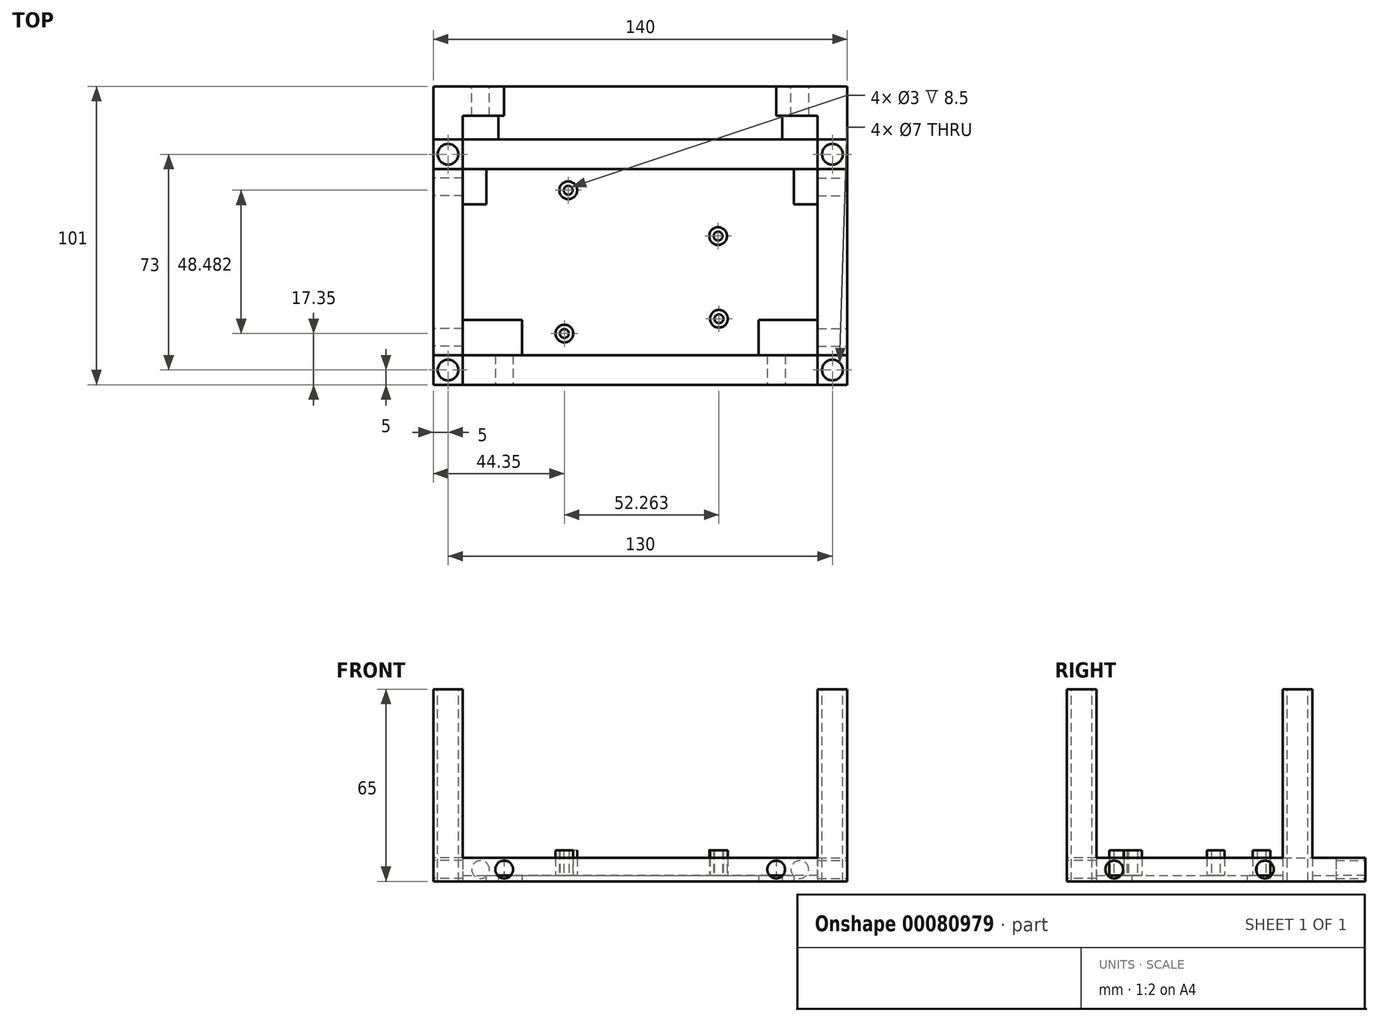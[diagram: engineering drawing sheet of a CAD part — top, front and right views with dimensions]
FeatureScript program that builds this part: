
annotation { "Feature Type Name" : "Feature", "Feature Type Description" : "" }
export const myFeature = defineFeature(function(context is Context, id is Id, definition is map)
    precondition{}
    {
        {
            var Q0;
            Q0=qCreatedBy(makeId("Top.planeOp"),FACE);
            var sketch = newSketch(context, id + "F0", { "sketchPlane" : qUnion([Q0])});
            skLineSegment(sketch, "E0.bottom", {"start": v(-70, 50) * mm, "end": v(70, 50) * mm, "construction": true});
            skLineSegment(sketch, "E0.top", {"start": v(-70, -50) * mm, "end": v(70, -50) * mm, "construction": true});
            skLineSegment(sketch, "E0.left", {"start": v(-70, 50) * mm, "end": v(-70, -50) * mm, "construction": true});
            skLineSegment(sketch, "E0.right", {"start": v(70, 50) * mm, "end": v(70, -50) * mm, "construction": true});
            skPoint(sketch, "E0.middle", {"position": v(0, 0) * mm});
            skLineSegment(sketch, "E1", {"start": v(-70, 50) * mm, "end": v(-70, 33) * mm});
            skLineSegment(sketch, "E2.bottom", {"start": v(-70, 33) * mm, "end": v(-60, 33) * mm});
            skLineSegment(sketch, "E2.top", {"start": v(-70, 23) * mm, "end": v(-60, 23) * mm});
            skLineSegment(sketch, "E2.left", {"start": v(-70, 33) * mm, "end": v(-70, 23) * mm});
            skLineSegment(sketch, "E2.right", {"start": v(-60, 33) * mm, "end": v(-60, 23) * mm});
            skLineSegment(sketch, "E3", {"start": v(70, 50) * mm, "end": v(70, 33) * mm});
            skLineSegment(sketch, "E4.bottom", {"start": v(70, 33) * mm, "end": v(60, 33) * mm});
            skLineSegment(sketch, "E4.top", {"start": v(70, 23) * mm, "end": v(60, 23) * mm});
            skLineSegment(sketch, "E4.left", {"start": v(70, 33) * mm, "end": v(70, 23) * mm});
            skLineSegment(sketch, "E4.right", {"start": v(60, 33) * mm, "end": v(60, 23) * mm});
            skLineSegment(sketch, "E5.bottom", {"start": v(-70, -50) * mm, "end": v(-60, -50) * mm});
            skLineSegment(sketch, "E5.top", {"start": v(-70, -40) * mm, "end": v(-60, -40) * mm});
            skLineSegment(sketch, "E5.left", {"start": v(-70, -50) * mm, "end": v(-70, -40) * mm});
            skLineSegment(sketch, "E5.right", {"start": v(-60, -50) * mm, "end": v(-60, -40) * mm});
            skLineSegment(sketch, "E6.bottom", {"start": v(70, -50) * mm, "end": v(60, -50) * mm});
            skLineSegment(sketch, "E6.top", {"start": v(70, -40) * mm, "end": v(60, -40) * mm});
            skLineSegment(sketch, "E6.left", {"start": v(70, -50) * mm, "end": v(70, -40) * mm});
            skLineSegment(sketch, "E6.right", {"start": v(60, -50) * mm, "end": v(60, -40) * mm});
            skSolve(sketch);
        }
        {
            var Q0;
            Q0=qSketchRegion(id+"F0",true);
            extrude(context, id + "F1", {"entities" : qUnion([Q0]), "oppositeDirection" : true, "depth" : 60 * mm});
        }
        {
            var Q0;
            Q0=qCreatedBy(makeId("Top.planeOp"),FACE);
            cPlane(context, id + "F2", {"entities" : qUnion([Q0]), "cplaneType" : CPlaneType.OFFSET, "offset" : 65 * mm, "oppositeDirection" : true, "width" : 150 * mm, "height" : 150 * mm});
        }
        {
            var Q0;
            Q0=qCreatedBy(id+"F2.planeOp",FACE);
            var sketch = newSketch(context, id + "F3", { "sketchPlane" : qUnion([Q0])});
            skLineSegment(sketch, "E7.0", {"start": v(-70, 33) * mm, "end": v(-60, 33) * mm});
            skLineSegment(sketch, "E8.0", {"start": v(-70, 33) * mm, "end": v(-70, 23) * mm});
            skLineSegment(sketch, "E9.0", {"start": v(-70, -50) * mm, "end": v(-70, -40) * mm});
            skLineSegment(sketch, "E10.0", {"start": v(-70, -50) * mm, "end": v(-60, -50) * mm});
            skLineSegment(sketch, "E11.0", {"start": v(70, -50) * mm, "end": v(60, -50) * mm});
            skLineSegment(sketch, "E12.0", {"start": v(70, -50) * mm, "end": v(70, -40) * mm});
            skLineSegment(sketch, "E13.0", {"start": v(70, 33) * mm, "end": v(70, 23) * mm});
            skLineSegment(sketch, "E14.0.0", {"start": v(70, 23) * mm, "end": v(70, 33) * mm});
            skLineSegment(sketch, "E14.0.1", {"start": v(70, 33) * mm, "end": v(60, 33) * mm});
            skLineSegment(sketch, "E15.0.0", {"start": v(-60, 33) * mm, "end": v(-70, 33) * mm});
            skLineSegment(sketch, "E16.0.0", {"start": v(-70, -40) * mm, "end": v(-70, -50) * mm});
            skLineSegment(sketch, "E17.0.0", {"start": v(60, -50) * mm, "end": v(70, -50) * mm});
            skLineSegment(sketch, "E18", {"start": v(-60, -50) * mm, "end": v(60, -50) * mm});
            skLineSegment(sketch, "E19", {"start": v(70, -40) * mm, "end": v(70, 23) * mm});
            skLineSegment(sketch, "E20", {"start": v(60, 33) * mm, "end": v(-60, 33) * mm});
            skLineSegment(sketch, "E21", {"start": v(-60, 23) * mm, "end": v(60, 23) * mm});
            skLineSegment(sketch, "E22", {"start": v(60, -40) * mm, "end": v(60, 23) * mm});
            skLineSegment(sketch, "E23", {"start": v(60, -40) * mm, "end": v(-60, -40) * mm});
            skLineSegment(sketch, "E24", {"start": v(-60, -40) * mm, "end": v(-60, 23) * mm});
            skLineSegment(sketch, "E25", {"start": v(-70, 23) * mm, "end": v(-70, -40) * mm});
            skPoint(sketch, "E14.0.2.end.orphan", {"position": v(60, 23) * mm});
            skLineSegment(sketch, "E26.top", {"start": v(-70, 51) * mm, "end": v(-60, 51) * mm});
            skLineSegment(sketch, "E26.left", {"start": v(-70, 33) * mm, "end": v(-70, 51) * mm});
            skLineSegment(sketch, "E26.right", {"start": v(-60, 33) * mm, "end": v(-60, 51) * mm});
            skLineSegment(sketch, "E27.top", {"start": v(70, 51) * mm, "end": v(60, 51) * mm});
            skLineSegment(sketch, "E27.left", {"start": v(70, 33) * mm, "end": v(70, 51) * mm});
            skLineSegment(sketch, "E27.right", {"start": v(60, 33) * mm, "end": v(60, 51) * mm});
            skLineSegment(sketch, "E28.bottom", {"start": v(-70, 51) * mm, "end": v(-46, 51) * mm});
            skLineSegment(sketch, "E28.top", {"start": v(-70, 41) * mm, "end": v(-46, 41) * mm});
            skLineSegment(sketch, "E28.left", {"start": v(-70, 51) * mm, "end": v(-70, 41) * mm});
            skLineSegment(sketch, "E28.right", {"start": v(-46, 51) * mm, "end": v(-46, 41) * mm});
            skLineSegment(sketch, "E29.bottom", {"start": v(70, 51) * mm, "end": v(46, 51) * mm});
            skLineSegment(sketch, "E29.top", {"start": v(70, 41) * mm, "end": v(46, 41) * mm});
            skLineSegment(sketch, "E29.left", {"start": v(70, 51) * mm, "end": v(70, 41) * mm});
            skLineSegment(sketch, "E29.right", {"start": v(46, 51) * mm, "end": v(46, 41) * mm});
            skSolve(sketch);
        }
        {
            var Q0;
            Q0=qSketchRegion(id+"F3",true);
            extrude(context, id + "F4", {"entities" : qUnion([Q0]), "operationType" : NewBodyOperationType.ADD, "depth" : 8 * mm});
        }
        {
            var Q0;
            Q0=qCreatedBy(id+"F2.planeOp",FACE);
            var sketch = newSketch(context, id + "F5", { "sketchPlane" : qUnion([Q0])});
            skPoint(sketch, "E30.0", {"position": v(-70, 33) * mm});
            skPoint(sketch, "E31.0", {"position": v(70, 33) * mm});
            skPoint(sketch, "E32.0", {"position": v(70, -50) * mm});
            skPoint(sketch, "E33.0", {"position": v(-70, -50) * mm});
            skPoint(sketch, "E34.0", {"position": v(-60, -40) * mm});
            skPoint(sketch, "E35.0", {"position": v(-60, 23) * mm});
            skPoint(sketch, "E36.0", {"position": v(60, 23) * mm});
            skPoint(sketch, "E37.0", {"position": v(60, -40) * mm});
            skLineSegment(sketch, "E38.bottom", {"start": v(-52, 33) * mm, "end": v(-48, 33) * mm});
            skLineSegment(sketch, "E39.top", {"start": v(60, -28) * mm, "end": v(40, -28) * mm});
            skLineSegment(sketch, "E39.right", {"start": v(40, -40) * mm, "end": v(40, -28) * mm});
            skLineSegment(sketch, "E40.top", {"start": v(60, 11) * mm, "end": v(52, 11) * mm});
            skLineSegment(sketch, "E41.top", {"start": v(-60, 11) * mm, "end": v(-52, 11) * mm});
            skLineSegment(sketch, "E42.top", {"start": v(-60, -28) * mm, "end": v(-40, -28) * mm});
            skLineSegment(sketch, "E42.right", {"start": v(-40, -40) * mm, "end": v(-40, -28) * mm});
            skLineSegment(sketch, "E43.0", {"start": v(-60, 41) * mm, "end": v(-46, 41) * mm});
            skLineSegment(sketch, "E44.0", {"start": v(-46, 51) * mm, "end": v(-46, 41) * mm});
            skLineSegment(sketch, "E45.0", {"start": v(46, 51) * mm, "end": v(46, 41) * mm});
            skLineSegment(sketch, "E46", {"start": v(-48, 33) * mm, "end": v(-48, 41) * mm});
            skLineSegment(sketch, "E47", {"start": v(-46, 51) * mm, "end": v(46, 51) * mm});
            skLineSegment(sketch, "E48", {"start": v(48, 33) * mm, "end": v(48, 41) * mm});
            skLineSegment(sketch, "E49", {"start": v(48, 33) * mm, "end": v(52, 33) * mm});
            skPoint(sketch, "E50.end.orphan", {"position": v(60, 41) * mm});
            skLineSegment(sketch, "E51", {"start": v(-60, -28) * mm, "end": v(-60, 11) * mm});
            skLineSegment(sketch, "E52", {"start": v(60, -28) * mm, "end": v(60, 11) * mm});
            skLineSegment(sketch, "E53", {"start": v(52, 33) * mm, "end": v(52, 11) * mm});
            skLineSegment(sketch, "E54", {"start": v(-52, 11) * mm, "end": v(-52, 33) * mm});
            skLineSegment(sketch, "E55", {"start": v(-40, -40) * mm, "end": v(40, -40) * mm});
            skLineSegment(sketch, "E56", {"start": v(46, 41) * mm, "end": v(48, 41) * mm});
            skLineSegment(sketch, "E57", {"start": v(-48, 41) * mm, "end": v(-46, 41) * mm});
            skSolve(sketch);
        }
        {
            var Q0;
            Q0=qSketchRegion(id+"F5",true);
            extrude(context, id + "F6", {"entities" : qUnion([Q0]), "operationType" : NewBodyOperationType.ADD, "depth" : 2 * mm});
        }
        {
            var Q0;
            Q0=qCreatedBy(id+"F2.planeOp",FACE);
            var sketch = newSketch(context, id + "F7", { "sketchPlane" : qUnion([Q0])});
            skLineSegment(sketch, "E58", {"start": v(-24.36, -18.42) * mm, "end": v(-24.36, -17.12) * mm, "construction": true});
            skPoint(sketch, "E59.middle", {"position": v(0, -8.5) * mm});
            skCircle(sketch, "E60", {"center": v(-24.35, 15.83) * mm, "radius": 1.5 * mm});
            skCircle(sketch, "E61", {"center": v(-25.65, -32.65) * mm, "radius": 1.5 * mm});
            skCircle(sketch, "E62", {"center": v(26.34, 0.33) * mm, "radius": 1.5 * mm});
            skCircle(sketch, "E63", {"center": v(26.61, -27.67) * mm, "radius": 1.5 * mm});
            skCircle(sketch, "E64", {"center": v(-24.35, 15.83) * mm, "radius": 3 * mm});
            skCircle(sketch, "E65", {"center": v(26.34, 0.33) * mm, "radius": 3 * mm});
            skCircle(sketch, "E66", {"center": v(26.61, -27.67) * mm, "radius": 3 * mm});
            skCircle(sketch, "E67", {"center": v(-25.65, -32.65) * mm, "radius": 3 * mm});
            skLineSegment(sketch, "E68", {"start": v(-24.35, 15.83) * mm, "end": v(26.34, 0.33) * mm, "construction": true});
            skLineSegment(sketch, "E69", {"start": v(26.34, 0.33) * mm, "end": v(26.61, -27.67) * mm, "construction": true});
            skLineSegment(sketch, "E70", {"start": v(26.61, -27.67) * mm, "end": v(-25.65, -32.65) * mm, "construction": true});
            skLineSegment(sketch, "E71", {"start": v(-25.65, -32.65) * mm, "end": v(-24.35, 15.83) * mm, "construction": true});
            skLineSegment(sketch, "E72", {"start": v(-24.35, 15.83) * mm, "end": v(26.61, -27.67) * mm, "construction": true});
            skLineSegment(sketch, "E73", {"start": v(26.34, 0.33) * mm, "end": v(-25.65, -32.65) * mm, "construction": true});
            skSolve(sketch);
        }
        {
            var Q0;
            Q0 = qSketchRegion(id + "F7", true);
            extrude(context, id + "F8", {"entities" : qUnion([Q0]), "operationType" : NewBodyOperationType.ADD, "depth" : 10.5 * mm});
        }
        {
            var Q0;
            Q0=qCreatedBy(makeId("Top.planeOp"),FACE);
            var sketch = newSketch(context, id + "F9", { "sketchPlane" : qUnion([Q0])});
            skLineSegment(sketch, "E74.0", {"start": v(-60, 33) * mm, "end": v(-60, 23) * mm});
            skLineSegment(sketch, "E75.0", {"start": v(-70, 23) * mm, "end": v(-60, 23) * mm});
            skLineSegment(sketch, "E76.0", {"start": v(-70, -40) * mm, "end": v(-60, -40) * mm});
            skLineSegment(sketch, "E77.0", {"start": v(-60, -50) * mm, "end": v(-60, -40) * mm});
            skLineSegment(sketch, "E78.0", {"start": v(60, -50) * mm, "end": v(60, -40) * mm});
            skLineSegment(sketch, "E79.0", {"start": v(70, -40) * mm, "end": v(60, -40) * mm});
            skLineSegment(sketch, "E80.0", {"start": v(70, 23) * mm, "end": v(60, 23) * mm});
            skLineSegment(sketch, "E81.0", {"start": v(60, 33) * mm, "end": v(60, 23) * mm});
            skCircle(sketch, "E82", {"center": v(-65, 28) * mm, "radius": 3.5 * mm});
            skPoint(sketch, "E82.centerSnap0", {"position": v(-60, 28) * mm});
            skPoint(sketch, "E82.centerSnap1", {"position": v(-65, 23) * mm});
            skCircle(sketch, "E83", {"center": v(-65, -45) * mm, "radius": 3.5 * mm});
            skPoint(sketch, "E83.centerSnap0", {"position": v(-60, -45) * mm});
            skPoint(sketch, "E83.centerSnap1", {"position": v(-65, -40) * mm});
            skCircle(sketch, "E84", {"center": v(65, -45) * mm, "radius": 3.5 * mm});
            skPoint(sketch, "E84.centerSnap0", {"position": v(60, -45) * mm});
            skPoint(sketch, "E84.centerSnap1", {"position": v(65, -40) * mm});
            skCircle(sketch, "E85", {"center": v(65, 28) * mm, "radius": 3.5 * mm});
            skPoint(sketch, "E85.centerSnap0", {"position": v(65, 23) * mm});
            skPoint(sketch, "E85.centerSnap1", {"position": v(60, 28) * mm});
            skSolve(sketch);
        }
        {
            var Q0;
            Q0 = qSketchRegion(id + "F9", true);
            extrude(context, id + "F10", {"entities" : qUnion([Q0]), "operationType" : NewBodyOperationType.REMOVE, "oppositeDirection" : true, "depth" : 75 * mm});
        }
        {
            var Q0;
            Q0=makeQuery(id+"F4.boolean.opBoolean","MERGE",FACE,{"derivedFrom":[makeQuery(id+"F1.opExtrude","SWEPT_FACE",FACE,{"disambiguationData":[OSD([sQuery(id+"F0.wireOp",EDGE,"E4.left")])]}),makeQuery(id+"F1.opExtrude","SWEPT_FACE",FACE,{"disambiguationData":[OSD([sQuery(id+"F0.wireOp",EDGE,"E6.left")])]}),makeQuery(id+"F4.opExtrude","SWEPT_FACE",FACE,{"disambiguationData":[OSD([sQuery(id+"F3.wireOp",EDGE,"E14.0.0"),sQuery(id+"F3.wireOp",EDGE,"E12.0"),sQuery(id+"F3.wireOp",EDGE,"E19"),sQuery(id+"F3.wireOp",EDGE,"E27.left"),sQuery(id+"F3.wireOp",EDGE,"E29.left")])]})]});
            var sketch = newSketch(context, id + "F11", { "sketchPlane" : qUnion([Q0])});
            skLineSegment(sketch, "E86", {"start": v(-40, -57) * mm, "end": v(-40, -65) * mm});
            skLineSegment(sketch, "E87.bottom", {"start": v(-40, -57) * mm, "end": v(-28, -57) * mm});
            skLineSegment(sketch, "E88.bottom", {"start": v(23, -57) * mm, "end": v(11, -57) * mm});
            skLineSegment(sketch, "E88.right", {"start": v(11, -57) * mm, "end": v(11, -65) * mm});
            skCircle(sketch, "E89", {"center": v(-34, -61) * mm, "radius": 3 * mm});
            skPoint(sketch, "E89.centerSnap0", {"position": v(-40, -61) * mm});
            skPoint(sketch, "E89.centerSnap1", {"position": v(-34, -57) * mm});
            skCircle(sketch, "E90", {"center": v(17, -61) * mm, "radius": 3 * mm});
            skPoint(sketch, "E90.centerSnap0", {"position": v(11, -61) * mm});
            skPoint(sketch, "E90.centerSnap1", {"position": v(17, -57) * mm});
            skSolve(sketch);
        }
        {
            var Q0;
            Q0 = qSketchRegion(id + "F11", true);
            extrude(context, id + "F12", {"entities" : qUnion([Q0]), "operationType" : NewBodyOperationType.REMOVE, "oppositeDirection" : true, "depth" : 10 * mm});
        }
        {
            var Q0;
            Q0=makeQuery(id+"F4.boolean.opBoolean","MERGE",FACE,{"derivedFrom":[makeQuery(id+"F1.opExtrude","SWEPT_FACE",FACE,{"disambiguationData":[OSD([sQuery(id+"F0.wireOp",EDGE,"E2.left")])]}),makeQuery(id+"F1.opExtrude","SWEPT_FACE",FACE,{"disambiguationData":[OSD([sQuery(id+"F0.wireOp",EDGE,"E5.left")])]}),makeQuery(id+"F4.opExtrude","SWEPT_FACE",FACE,{"disambiguationData":[OSD([sQuery(id+"F3.wireOp",EDGE,"E8.0"),sQuery(id+"F3.wireOp",EDGE,"E16.0.0"),sQuery(id+"F3.wireOp",EDGE,"E25"),sQuery(id+"F3.wireOp",EDGE,"E26.left"),sQuery(id+"F3.wireOp",EDGE,"E28.left")])]})]});
            var sketch = newSketch(context, id + "F13", { "sketchPlane" : qUnion([Q0])});
            skLineSegment(sketch, "E91", {"start": v(-23, -57) * mm, "end": v(-11, -57) * mm});
            skLineSegment(sketch, "E92", {"start": v(-11, -57) * mm, "end": v(-11, -65) * mm});
            skLineSegment(sketch, "E93", {"start": v(40, -57) * mm, "end": v(28, -57) * mm});
            skLineSegment(sketch, "E94", {"start": v(28, -57) * mm, "end": v(28, -65) * mm});
            skCircle(sketch, "E95", {"center": v(-17, -61) * mm, "radius": 3 * mm});
            skPoint(sketch, "E95.centerSnap0", {"position": v(-11, -61) * mm});
            skPoint(sketch, "E95.centerSnap1", {"position": v(-17, -57) * mm});
            skCircle(sketch, "E96", {"center": v(34, -61) * mm, "radius": 3 * mm});
            skPoint(sketch, "E96.centerSnap0", {"position": v(28, -61) * mm});
            skPoint(sketch, "E96.centerSnap1", {"position": v(34, -57) * mm});
            skSolve(sketch);
        }
        {
            var Q0;
            Q0 = qSketchRegion(id + "F13", true);
            extrude(context, id + "F14", {"entities" : qUnion([Q0]), "operationType" : NewBodyOperationType.REMOVE, "oppositeDirection" : true, "depth" : 10 * mm});
        }
        {
            var Q0;
            Q0=makeQuery(id+"F4.boolean.opBoolean","MERGE",FACE,{"derivedFrom":[makeQuery(id+"F1.opExtrude","SWEPT_FACE",FACE,{"disambiguationData":[OSD([sQuery(id+"F0.wireOp",EDGE,"E5.bottom")])]}),makeQuery(id+"F1.opExtrude","SWEPT_FACE",FACE,{"disambiguationData":[OSD([sQuery(id+"F0.wireOp",EDGE,"E6.bottom")])]}),makeQuery(id+"F4.opExtrude","SWEPT_FACE",FACE,{"disambiguationData":[OSD([sQuery(id+"F3.wireOp",EDGE,"E10.0"),sQuery(id+"F3.wireOp",EDGE,"E17.0.0"),sQuery(id+"F3.wireOp",EDGE,"E18")])]})]});
            var sketch = newSketch(context, id + "F15", { "sketchPlane" : qUnion([Q0])});
            skCircle(sketch, "E97", {"center": v(-46, -61) * mm, "radius": 3 * mm});
            skCircle(sketch, "E98", {"center": v(46, -61) * mm, "radius": 3 * mm});
            skLineSegment(sketch, "E99", {"start": v(-60, -57) * mm, "end": v(-46, -57) * mm});
            skLineSegment(sketch, "E100", {"start": v(-46, -57) * mm, "end": v(-46, -61) * mm});
            skLineSegment(sketch, "E101", {"start": v(60, -57) * mm, "end": v(46, -57) * mm});
            skLineSegment(sketch, "E102", {"start": v(46, -57) * mm, "end": v(46, -61) * mm});
            skSolve(sketch);
        }
        {
            var Q0;
            Q0 = qSketchRegion(id + "F15", true);
            extrude(context, id + "F16", {"entities" : qUnion([Q0]), "operationType" : NewBodyOperationType.REMOVE, "oppositeDirection" : true, "depth" : 10 * mm});
        }
        {
            var Q0;
            Q0=makeQuery(id+"F4.opExtrude","SWEPT_FACE",FACE,{"disambiguationData":[OSD([sQuery(id+"F3.wireOp",EDGE,"E28.bottom")])]});
            var sketch = newSketch(context, id + "F17", { "sketchPlane" : qUnion([Q0])});
            skCircle(sketch, "E103", {"center": v(-54, -61) * mm, "radius": 3 * mm});
            skCircle(sketch, "E104", {"center": v(54, -61) * mm, "radius": 3 * mm});
            skPoint(sketch, "E105.0", {"position": v(-70, -57) * mm});
            skPoint(sketch, "E106.0", {"position": v(70, -57) * mm});
            skLineSegment(sketch, "E107", {"start": v(-70, -57) * mm, "end": v(-54, -57) * mm});
            skLineSegment(sketch, "E108", {"start": v(-54, -57) * mm, "end": v(-54, -61) * mm});
            skLineSegment(sketch, "E109", {"start": v(70, -57) * mm, "end": v(54, -57) * mm});
            skLineSegment(sketch, "E110", {"start": v(54, -57) * mm, "end": v(54, -61) * mm});
            skSolve(sketch);
        }
        {
            var Q0;
            Q0 = qSketchRegion(id + "F17", true);
            extrude(context, id + "F18", {"entities" : qUnion([Q0]), "operationType" : NewBodyOperationType.REMOVE, "oppositeDirection" : true, "depth" : 10 * mm});
        }
    });
